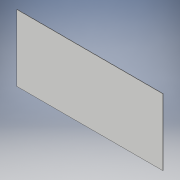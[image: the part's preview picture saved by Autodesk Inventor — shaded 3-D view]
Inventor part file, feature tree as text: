
AUTODESK INVENTOR PART (.ipt)
format: ipt  version: 2017 (Build 210142000, 142)  size: 87,040 bytes
history: native  units: in
note: dims shown in document units (in); Inventor stores cm internally (conversion verified against a paired STEP export)
features: extrude x1, sketch x1
ambient origin geometry x8: Origin, YZ Plane, XZ Plane, XY Plane, X Axis, Y Axis, Z Axis, Center Point
bodies: Solid1 (feature_tree)
feature tree (2):
  extrude  "Extrusion1"  Depth=11.0in
  sketch  "Sketch1"  dims[d0=5.0in d1=11.0in d2=0.025in d3=0.0in]
